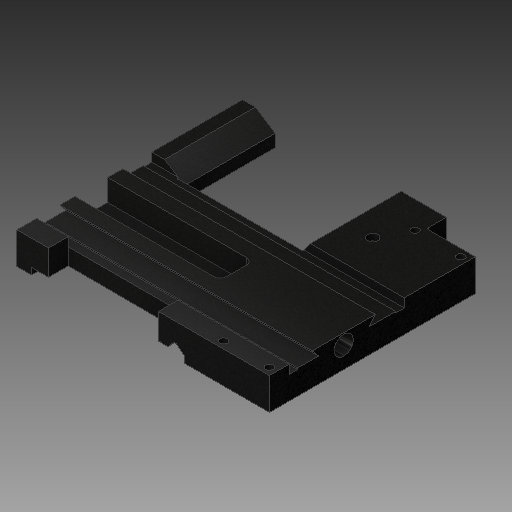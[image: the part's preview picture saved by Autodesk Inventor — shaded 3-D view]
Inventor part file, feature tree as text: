
AUTODESK INVENTOR PART (.ipt)
format: ipt  version: 2018 (Build 220112000, 112)  size: 342,016 bytes
history: native  units: in
note: dims shown in document units (in); Inventor stores cm internally (conversion verified against a paired STEP export)
features: extrude x14, sketch x9
ambient origin geometry x8: Origin, YZ Plane, XZ Plane, XY Plane, X Axis, Y Axis, Z Axis, Center Point
bodies: Solid1 (feature_tree)
feature tree (23):
  extrude  "Extrusion1"  Depth=13.5039in
  extrude  "Extrusion2"  Depth=1.9094in TaperAngle=0.0deg
  extrude  "Extrusion3"  Depth=1.378in
  extrude  "Extrusion4"  Depth=0.8933in
  extrude  "Extrusion8"  Depth=0.0787in
  extrude  "Extrusion19"  Depth=1.1811in
  extrude  "Extrusion21"  Depth=0.1181in
  extrude  "Extrusion22"  Depth=0.3937in
  extrude  "Extrusion23"  Depth=6.5748in
  extrude  "Extrusion24"  Depth=6.5748in
  extrude  "Extrusion25"  Depth=6.5748in
  extrude  "Extrusion26"  Depth=6.5748in
  extrude  "Extrusion27"  TaperAngle=0.0deg  [1 undecoded]
  extrude  "Extrusion28"  Depth=0.0787in TaperAngle=0.0deg
  sketch  "Sketch1"  dims[d0=15.1181in d1=13.5039in]
  sketch  "Sketch12"  dims[d2=1.9094in d3=0.0in d12=1.9094in d13=0.0in]
  sketch  "Sketch28"  dims[d23=1.378in d27=3.7795in]
  sketch  "Sketch32"  dims[d29=1.7323in d32=0.8933in]
  sketch  "Sketch36"  dims[d35=1.9094in d36=0.0in d37=0.0787in]
  sketch  "Sketch38"  dims[d38=0.5118in d43=1.1811in]
  sketch  "Sketch40"  dims[d44=1.9094in d45=0.0in d46=0.1181in]
  sketch  "Sketch41"  dims[d52=0.3436in d72=0.3937in]
  sketch  "Sketch42"  dims[d73=1.2992in d74=0.0in d146=0.4567in d149=0.4567in d152=0.4567in d155=0.4567in d156=0.0in d157=0.0in d161=0.0787in d162=0.0in d168=0.6299in d169=0.3937in d170=0.0in d209=0.6299in d210=45.0deg d211=0.1811in d214=0.5197in d215=45.0deg d216=0.4724in d224=0.8661in d225=0.3937in d227=0.3937in d228=0.0in d229=0.5512in d232=0.748in d233=5.5118in d234=0.0in d235=5.5118in d236=0.0in d240=0.5197in d242=0.1811in d243=0.6299in d245=5.5118in d246=0.0in d247=0.6693in d248=0.3937in d249=0.0in d250=1.1417in d251=2.2441in d252=0.0in d255=1.8898in d256=6.5748in]
note: 1 required parameter value undecoded (feature->parameter linkage not recoverable at this tier; creation-order binding heuristic only, values carry confidence <= 0.55)
